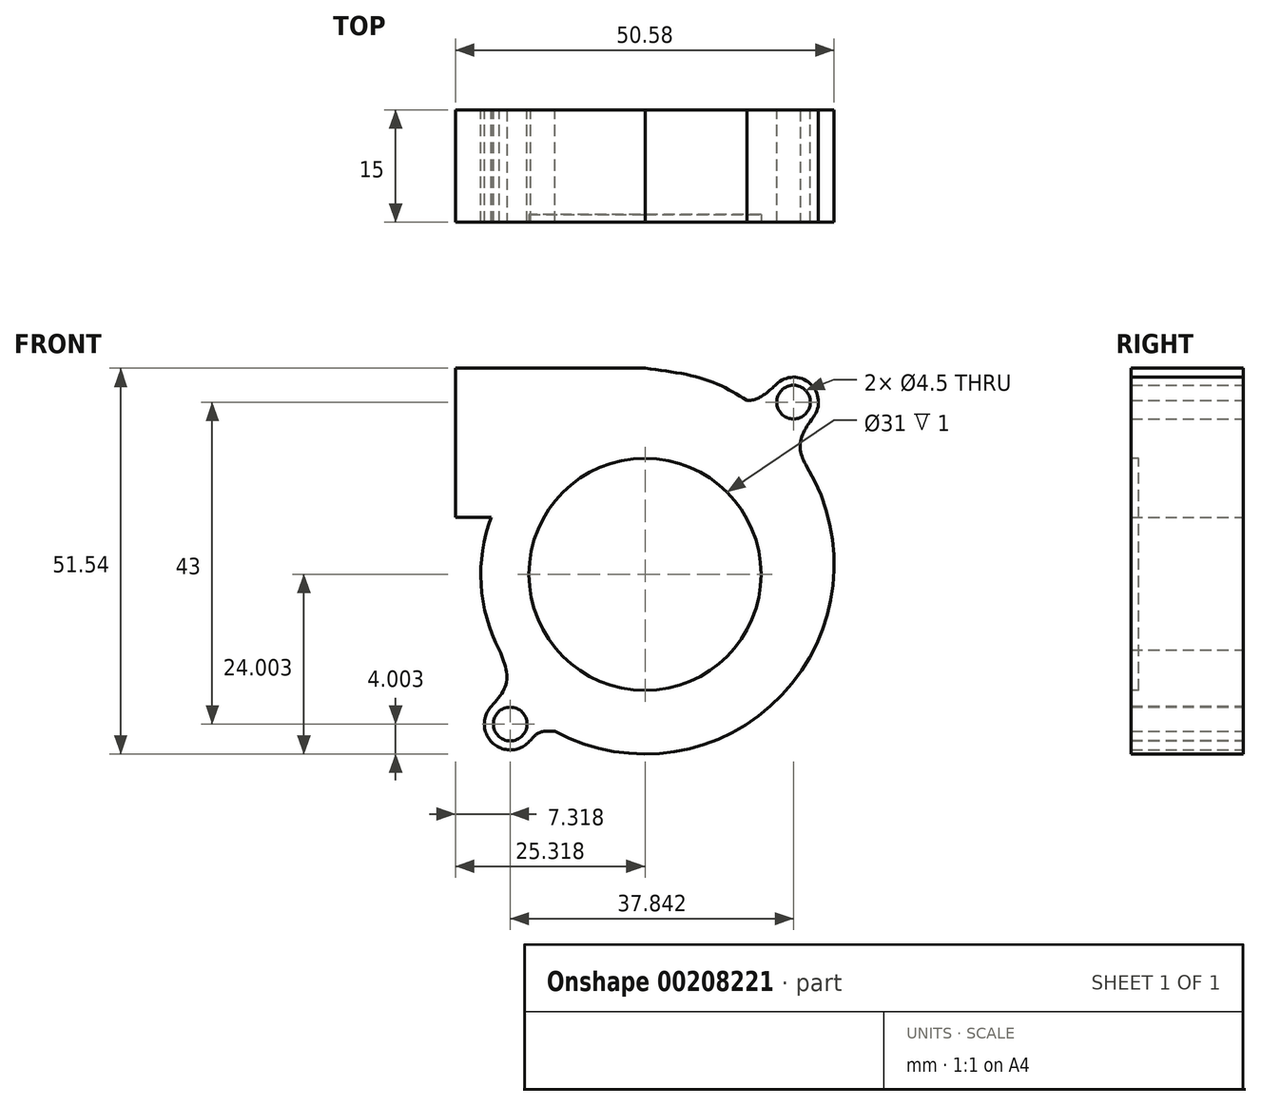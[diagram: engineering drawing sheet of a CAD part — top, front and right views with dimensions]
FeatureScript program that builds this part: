
annotation { "Feature Type Name" : "Feature", "Feature Type Description" : "" }
export const myFeature = defineFeature(function(context is Context, id is Id, definition is map)
    precondition{}
    {
        {
            var Q0;
            Q0=qCreatedBy(makeId("Front.planeOp"),FACE);
            var sketch = newSketch(context, id + "F0", { "sketchPlane" : qUnion([Q0])});
            skLineSegment(sketch, "E0", {"start": v(25, 21.86) * mm, "end": v(76, 21.86) * mm, "construction": true});
            skCircle(sketch, "E1", {"center": v(32.35, -50.43) * mm, "radius": 2.25 * mm});
            skPoint(sketch, "E1.first.point", {"position": v(33.81, -48.72) * mm});
            skPoint(sketch, "E1.second.point", {"position": v(30.23, -49.67) * mm});
            skPoint(sketch, "E1.third.point", {"position": v(33.18, -52.52) * mm});
            skCircle(sketch, "E2", {"center": v(70.2, -7.43) * mm, "radius": 2.25 * mm});
            skPoint(sketch, "E2.first.point", {"position": v(68.85, -5.62) * mm});
            skPoint(sketch, "E2.second.point", {"position": v(71.74, -9.05) * mm});
            skPoint(sketch, "E2.third.point", {"position": v(69.28, -9.48) * mm});
            skLineSegment(sketch, "E3", {"start": v(32.35, -50.43) * mm, "end": v(70.35, -50.43) * mm, "construction": true});
            skLineSegment(sketch, "E4", {"start": v(70.35, -50.43) * mm, "end": v(70.2, -7.43) * mm, "construction": true});
            skPoint(sketch, "E5", {"position": v(50.35, -50.43) * mm});
            skLineSegment(sketch, "E6", {"start": v(50.35, -50.43) * mm, "end": v(50.35, -3.8) * mm, "construction": true});
            skPoint(sketch, "E7", {"position": v(70.27, -30.43) * mm});
            skLineSegment(sketch, "E8", {"start": v(70.27, -30.43) * mm, "end": v(-9.64, -30.43) * mm, "construction": true});
            skCircle(sketch, "E9", {"center": v(50.35, -30.43) * mm, "radius": 15.5 * mm});
            skCircle(sketch, "E10", {"center": v(50.35, -30.43) * mm, "radius": 13 * mm});
            skLineSegment(sketch, "E11.top", {"start": v(50.14, -54.43) * mm, "end": v(75.95, -54.43) * mm});
            skPoint(sketch, "E12.first.point", {"position": v(60.87, -6.1) * mm});
            skPoint(sketch, "E12.second.point", {"position": v(74.01, -20.26) * mm});
            skPoint(sketch, "E12.third.point", {"position": v(50.45, -54.43) * mm});
            skArc(sketch, "E13", {"start": v(29.8, -22.79) * mm, "mid": v(28.46, -31.79) * mm, "end": v(30.9, -40.55) * mm});
            skArc(sketch, "E14", {"start": v(29.84, -48.05) * mm, "mid": v(30.09, -53.04) * mm, "end": v(35.07, -52.56) * mm});
            skArc(sketch, "E15", {"start": v(72.84, -9.44) * mm, "mid": v(72.4, -4.94) * mm, "end": v(67.87, -5.04) * mm});
            skFitSpline(sketch, "E16", {"points": [v(67.87, -5.04) * mm, v(64.66, -7.14) * mm, v(61.46, -6.39) * mm], "startDerivative": vector(-6.14, -5.95) * mm, "endDerivative": vector(-6.65, 3.27) * mm});
            skFitSpline(sketch, "E17", {"points": [v(72.84, -9.44) * mm, v(71.07, -12.96) * mm, v(71.98, -16.05) * mm], "startDerivative": vector(-5.34, -7) * mm, "endDerivative": vector(3.74, -6.22) * mm});
            skFitSpline(sketch, "E18", {"points": [v(34.84, -52.82) * mm, v(36.3, -51.55) * mm, v(38.3, -51.4) * mm], "startDerivative": vector(2.7, 3.13) * mm, "endDerivative": vector(4.24, -0.26) * mm});
            skFitSpline(sketch, "E19", {"points": [v(29.84, -48.05) * mm, v(31.86, -44.77) * mm, v(30.9, -40.55) * mm], "startDerivative": vector(5.6, 6.4) * mm, "endDerivative": vector(-3.37, 8.6) * mm});
            skArc(sketch, "E20.trimOffspring", {"start": v(38.3, -51.4) * mm, "mid": v(68.63, -46.57) * mm, "end": v(71.98, -16.05) * mm});
            skPoint(sketch, "E21.orphan", {"position": v(24.95, -54.43) * mm});
            skLineSegment(sketch, "E22.bottom", {"start": v(50.35, -2.89) * mm, "end": v(25.03, -2.89) * mm});
            skLineSegment(sketch, "E22.top", {"start": v(29.8, -22.79) * mm, "end": v(25.03, -22.79) * mm});
            skLineSegment(sketch, "E22.left", {"start": v(50.35, -2.89) * mm, "end": v(50.35, -22.79) * mm});
            skLineSegment(sketch, "E22.right", {"start": v(25.03, -2.89) * mm, "end": v(25.03, -22.79) * mm});
            skLineSegment(sketch, "E23.trimOffspring", {"start": v(50.35, -2.89) * mm, "end": v(50.35, 14) * mm, "construction": true});
            skFitSpline(sketch, "E24", {"points": [v(50.35, -2.89) * mm, v(58.6, -4.46) * mm, v(63.96, -7.18) * mm], "startDerivative": vector(16.18, -2.08) * mm, "endDerivative": vector(10.9, -6.62) * mm});
            skSolve(sketch);
        }
        {
            var Q0;
            Q0 = qSketchRegion(id + "F0", true);
            var Q1;
            Q1=makeQuery(id+"F0.imprint","IMPRINT",FACE,{"disambiguationData":[TD([[makeQuery(id+"F0.imprint","IMPRINT",EDGE,{"derivedFrom":sQuery(id+"F0.wireOp",EDGE,"E10")}),1.0]])]});
            var Q2;
            Q2=makeQuery(id+"F0.imprint","IMPRINT",FACE,{"disambiguationData":[TD([[makeQuery(id+"F0.imprint","IMPRINT",EDGE,{"derivedFrom":sQuery(id+"F0.wireOp",EDGE,"E9")}),1.0]])]});
            extrude(context, id + "F1", {"entities" : qUnion([Q0, Q1, Q2]), "depth" : 15 * mm});
        }
        {
            var Q0;
            Q0=makeQuery(id+"F1.opExtrude","CAP_FACE",FACE,{"disambiguationData":[OSD([sQuery(id+"F0.wireOp",EDGE,"E1"),sQuery(id+"F0.wireOp",EDGE,"E2"),sQuery(id+"F0.wireOp",EDGE,"E13"),sQuery(id+"F0.wireOp",EDGE,"E14"),sQuery(id+"F0.wireOp",EDGE,"E15"),sQuery(id+"F0.wireOp",EDGE,"E16"),sQuery(id+"F0.wireOp",EDGE,"E17"),sQuery(id+"F0.wireOp",EDGE,"E18"),sQuery(id+"F0.wireOp",EDGE,"E19"),sQuery(id+"F0.wireOp",EDGE,"E20.trimOffspring"),sQuery(id+"F0.wireOp",EDGE,"E22.bottom"),sQuery(id+"F0.wireOp",EDGE,"E22.top"),sQuery(id+"F0.wireOp",EDGE,"E22.right"),sQuery(id+"F0.wireOp",EDGE,"E24")])],"isStart":false});
            var sketch = newSketch(context, id + "F2", { "sketchPlane" : qUnion([Q0])});
            skCircle(sketch, "E25.0", {"center": v(50.35, -30.43) * mm, "radius": 15.5 * mm});
            skSolve(sketch);
        }
        {
            var Q0;
            Q0 = qSketchRegion(id + "F2", true);
            extrude(context, id + "F3", {"entities" : qUnion([Q0]), "operationType" : NewBodyOperationType.REMOVE, "oppositeDirection" : true, "depth" : 1 * mm});
        }
    });
